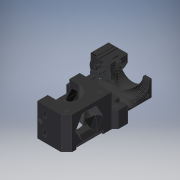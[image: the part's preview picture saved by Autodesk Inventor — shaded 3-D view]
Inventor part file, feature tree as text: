
AUTODESK INVENTOR PART (.ipt)
format: ipt  version: 2018 (Build 220112000, 112)  size: 4,322,304 bytes
history: native  units: mm
features: extrude x1, other x1
ambient origin geometry x8: Origin, YZ Plane, XZ Plane, XY Plane, X Axis, Y Axis, Z Axis, Center Point
bodies: Solid1 (feature_tree)
feature tree (2):
  extrude  "extrudertest"  [1 undecoded]
  other  "MeshFeature1"
note: 1 required parameter value undecoded (feature->parameter linkage not recoverable at this tier; creation-order binding heuristic only, values carry confidence <= 0.55)
